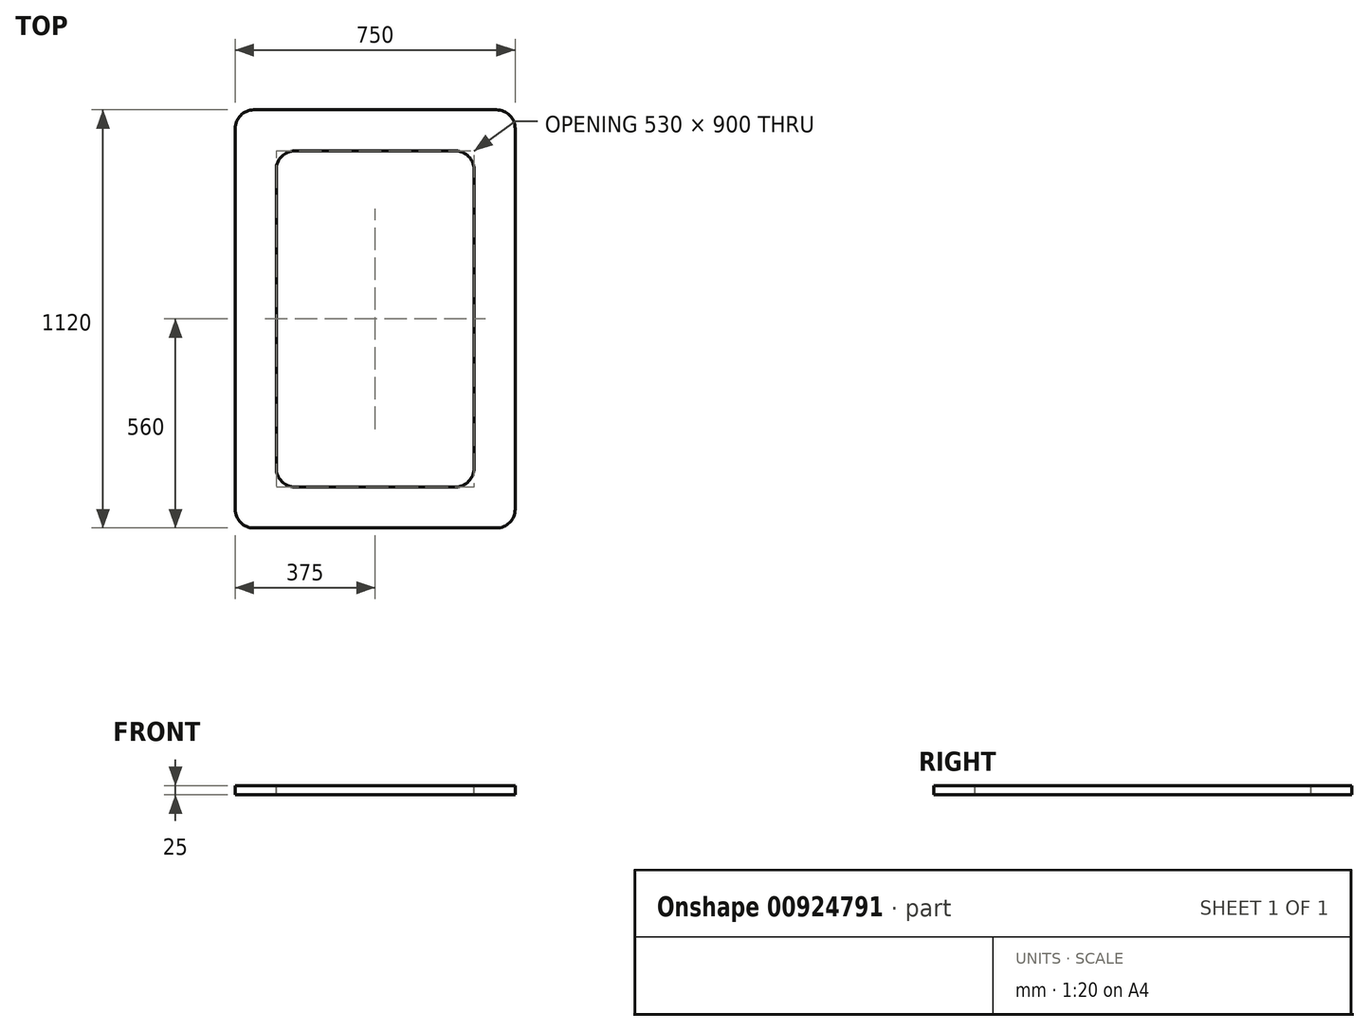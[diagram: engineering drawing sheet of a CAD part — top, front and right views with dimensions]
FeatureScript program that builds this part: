
annotation { "Feature Type Name" : "Feature", "Feature Type Description" : "" }
export const myFeature = defineFeature(function(context is Context, id is Id, definition is map)
    precondition{}
    {
        {
            var Q0;
            Q0=qCreatedBy(makeId("Top.planeOp"),FACE);
            var sketch = newSketch(context, id + "F0", { "sketchPlane" : qUnion([Q0])});
            skLineSegment(sketch, "E0.bottom", {"start": v(-325, 560) * mm, "end": v(325, 560) * mm});
            skLineSegment(sketch, "E0.top", {"start": v(-325, -560) * mm, "end": v(325, -560) * mm});
            skLineSegment(sketch, "E0.left", {"start": v(-375, 510) * mm, "end": v(-375, -510) * mm});
            skLineSegment(sketch, "E0.right", {"start": v(375, 510) * mm, "end": v(375, -510) * mm});
            skPoint(sketch, "E1.visualSharp", {"position": v(-375, 560) * mm});
            skArc(sketch, "E1.filletArc", {"start": v(-325, 560) * mm, "mid": v(-360.36, 545.36) * mm, "end": v(-375, 510) * mm});
            skPoint(sketch, "E2.visualSharp", {"position": v(375, 560) * mm});
            skArc(sketch, "E2.filletArc", {"start": v(375, 510) * mm, "mid": v(360.36, 545.36) * mm, "end": v(325, 560) * mm});
            skPoint(sketch, "E3.visualSharp", {"position": v(375, -560) * mm});
            skArc(sketch, "E3.filletArc", {"start": v(325, -560) * mm, "mid": v(360.36, -545.36) * mm, "end": v(375, -510) * mm});
            skPoint(sketch, "E4.visualSharp", {"position": v(-375, -560) * mm});
            skArc(sketch, "E4.filletArc", {"start": v(-375, -510) * mm, "mid": v(-360.36, -545.36) * mm, "end": v(-325, -560) * mm});
            skSolve(sketch);
        }
        {
            var Q0;
            Q0=makeQuery(id+"F0.imprint","IMPRINT",FACE,{"disambiguationData":[TD([[makeQuery(id+"F0.imprint","IMPRINT",EDGE,{"derivedFrom":sQuery(id+"F0.wireOp",EDGE,"E0.bottom")}),-1.0]])]});
            extrude(context, id + "F1", {"entities" : qUnion([Q0]), "depth" : 25 * mm, "offsetDistance" : 25 * mm});
        }
        {
            var Q0;
            Q0=makeQuery(id+"F1.opExtrude","CAP_FACE",FACE,{"disambiguationData":[OSD([sQuery(id+"F0.wireOp",EDGE,"E0.bottom"),sQuery(id+"F0.wireOp",EDGE,"E0.top"),sQuery(id+"F0.wireOp",EDGE,"E0.left"),sQuery(id+"F0.wireOp",EDGE,"E0.right"),sQuery(id+"F0.wireOp",EDGE,"E1.filletArc"),sQuery(id+"F0.wireOp",EDGE,"E2.filletArc"),sQuery(id+"F0.wireOp",EDGE,"E3.filletArc"),sQuery(id+"F0.wireOp",EDGE,"E4.filletArc")])],"isStart":false});
            var sketch = newSketch(context, id + "F2", { "sketchPlane" : qUnion([Q0])});
            skLineSegment(sketch, "E5.1", {"start": v(-215, 450) * mm, "end": v(215, 450) * mm});
            skLineSegment(sketch, "E5.2", {"start": v(-265, 400) * mm, "end": v(-265, -400) * mm});
            skLineSegment(sketch, "E5.5", {"start": v(-215, -450) * mm, "end": v(215, -450) * mm});
            skLineSegment(sketch, "E5.7", {"start": v(265, 400) * mm, "end": v(265, -400) * mm});
            skPoint(sketch, "E6.visualSharp", {"position": v(-265, 450) * mm});
            skArc(sketch, "E6.filletArc", {"start": v(-215, 450) * mm, "mid": v(-250.36, 435.36) * mm, "end": v(-265, 400) * mm});
            skPoint(sketch, "E7.visualSharp", {"position": v(265, 450) * mm});
            skArc(sketch, "E7.filletArc", {"start": v(265, 400) * mm, "mid": v(250.36, 435.36) * mm, "end": v(215, 450) * mm});
            skPoint(sketch, "E8.visualSharp", {"position": v(265, -450) * mm});
            skArc(sketch, "E8.filletArc", {"start": v(215, -450) * mm, "mid": v(250.36, -435.36) * mm, "end": v(265, -400) * mm});
            skPoint(sketch, "E9.visualSharp", {"position": v(-265, -450) * mm});
            skArc(sketch, "E9.filletArc", {"start": v(-265, -400) * mm, "mid": v(-250.36, -435.36) * mm, "end": v(-215, -450) * mm});
            skSolve(sketch);
        }
        {
            var Q0;
            Q0=makeQuery(id+"F2.imprint","IMPRINT",FACE,{"disambiguationData":[TD([[makeQuery(id+"F2.imprint","IMPRINT",EDGE,{"derivedFrom":sQuery(id+"F2.wireOp",EDGE,"E5.1")}),-1.0]])]});
            extrude(context, id + "F3", {"entities" : qUnion([Q0]), "operationType" : NewBodyOperationType.REMOVE, "oppositeDirection" : true, "depth" : 25 * mm, "offsetDistance" : 25 * mm});
        }
    });
